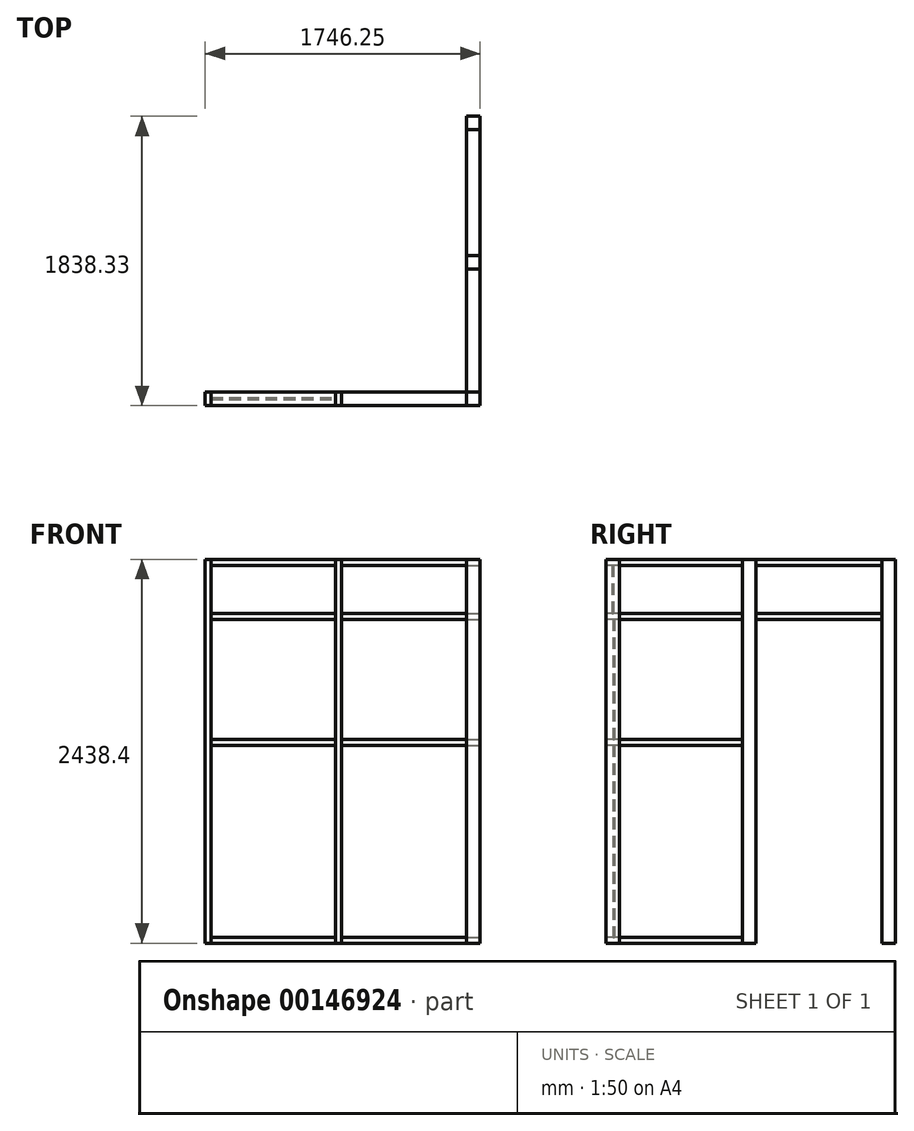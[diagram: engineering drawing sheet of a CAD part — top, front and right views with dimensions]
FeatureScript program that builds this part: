
annotation { "Feature Type Name" : "Feature", "Feature Type Description" : "" }
export const myFeature = defineFeature(function(context is Context, id is Id, definition is map)
    precondition{}
    {
        {
            var Q0;
            Q0=qCreatedBy(makeId("Top.planeOp"),FACE);
            var sketch = newSketch(context, id + "F0", { "sketchPlane" : qUnion([Q0])});
            skLineSegment(sketch, "E0.bottom", {"start": v(0, 0) * mm, "end": v(38.1, 0) * mm});
            skLineSegment(sketch, "E0.top", {"start": v(0, 85.73) * mm, "end": v(38.1, 85.73) * mm});
            skLineSegment(sketch, "E0.left", {"start": v(0, 0) * mm, "end": v(0, 85.73) * mm});
            skLineSegment(sketch, "E0.right", {"start": v(38.1, 0) * mm, "end": v(38.1, 85.73) * mm});
            skLineSegment(sketch, "E1", {"start": v(38.1, 0) * mm, "end": v(828.68, 0) * mm});
            skLineSegment(sketch, "E2.bottom", {"start": v(828.68, 0) * mm, "end": v(866.78, 0) * mm});
            skLineSegment(sketch, "E2.top", {"start": v(828.68, 85.73) * mm, "end": v(866.78, 85.73) * mm});
            skLineSegment(sketch, "E2.left", {"start": v(828.68, 0) * mm, "end": v(828.68, 85.73) * mm});
            skLineSegment(sketch, "E2.right", {"start": v(866.78, 0) * mm, "end": v(866.78, 85.73) * mm});
            skLineSegment(sketch, "E3", {"start": v(866.78, 0) * mm, "end": v(1660.53, 0) * mm});
            skLineSegment(sketch, "E4.bottom", {"start": v(1660.53, 0) * mm, "end": v(1746.25, 0) * mm});
            skLineSegment(sketch, "E4.top", {"start": v(1660.53, 85.73) * mm, "end": v(1746.25, 85.73) * mm});
            skLineSegment(sketch, "E4.left", {"start": v(1660.53, 0) * mm, "end": v(1660.53, 85.73) * mm});
            skLineSegment(sketch, "E4.right", {"start": v(1746.25, 0) * mm, "end": v(1746.25, 85.73) * mm});
            skLineSegment(sketch, "E5", {"start": v(1746.25, 85.72) * mm, "end": v(1746.25, 866.78) * mm});
            skLineSegment(sketch, "E6.bottom", {"start": v(1746.25, 866.78) * mm, "end": v(1660.53, 866.78) * mm});
            skLineSegment(sketch, "E6.top", {"start": v(1746.25, 952.5) * mm, "end": v(1660.53, 952.5) * mm});
            skLineSegment(sketch, "E6.left", {"start": v(1746.25, 866.78) * mm, "end": v(1746.25, 952.5) * mm});
            skLineSegment(sketch, "E6.right", {"start": v(1660.53, 866.78) * mm, "end": v(1660.53, 952.5) * mm});
            skLineSegment(sketch, "E7", {"start": v(1746.25, 952.5) * mm, "end": v(1746.25, 1752.6) * mm});
            skLineSegment(sketch, "E8.bottom", {"start": v(1746.25, 1752.6) * mm, "end": v(1660.52, 1752.6) * mm});
            skLineSegment(sketch, "E8.top", {"start": v(1746.25, 1838.33) * mm, "end": v(1660.53, 1838.33) * mm});
            skLineSegment(sketch, "E8.left", {"start": v(1746.25, 1752.6) * mm, "end": v(1746.25, 1838.33) * mm});
            skLineSegment(sketch, "E8.right", {"start": v(1660.52, 1752.6) * mm, "end": v(1660.52, 1838.33) * mm});
            skSolve(sketch);
        }
        {
            var Q0;
            Q0=makeQuery(id+"F0.imprint","IMPRINT",FACE,{"disambiguationData":[TD([[makeQuery(id+"F0.imprint","IMPRINT",EDGE,{"derivedFrom":sQuery(id+"F0.wireOp",EDGE,"E0.bottom")}),1.0]])]});
            var Q1;
            Q1=makeQuery(id+"F0.imprint","IMPRINT",FACE,{"disambiguationData":[TD([[makeQuery(id+"F0.imprint","IMPRINT",EDGE,{"derivedFrom":sQuery(id+"F0.wireOp",EDGE,"E2.bottom")}),1.0]])]});
            var Q2;
            Q2=makeQuery(id+"F0.imprint","IMPRINT",FACE,{"disambiguationData":[TD([[makeQuery(id+"F0.imprint","IMPRINT",EDGE,{"derivedFrom":sQuery(id+"F0.wireOp",EDGE,"E4.bottom")}),1.0]])]});
            var Q3;
            Q3=makeQuery(id+"F0.imprint","IMPRINT",FACE,{"disambiguationData":[TD([[makeQuery(id+"F0.imprint","IMPRINT",EDGE,{"derivedFrom":sQuery(id+"F0.wireOp",EDGE,"E6.bottom")}),-1.0]])]});
            var Q4;
            Q4=makeQuery(id+"F0.imprint","IMPRINT",FACE,{"disambiguationData":[TD([[makeQuery(id+"F0.imprint","IMPRINT",EDGE,{"derivedFrom":sQuery(id+"F0.wireOp",EDGE,"E8.bottom")}),-1.0]])]});
            extrude(context, id + "F1", {"entities" : qUnion([Q0, Q1, Q2, Q3, Q4]), "depth" : 2438.4 * mm});
        }
        {
            var Q0;
            Q0=makeQuery(id+"F1.opExtrude","SWEPT_FACE",FACE,{"disambiguationData":[OSD([sQuery(id+"F0.wireOp",EDGE,"E2.right")])]});
            var sketch = newSketch(context, id + "F2", { "sketchPlane" : qUnion([Q0])});
            skLineSegment(sketch, "E9", {"start": v(0, 0) * mm, "end": v(0, 38.1) * mm});
            skLineSegment(sketch, "E10", {"start": v(0, 38.1) * mm, "end": v(85.72, 38.1) * mm});
            skSolve(sketch);
        }
        {
            var Q0;
            Q0=makeQuery(id+"F1.opExtrude","SWEPT_FACE",FACE,{"disambiguationData":[OSD([sQuery(id+"F0.wireOp",EDGE,"E0.right")])]});
            var sketch = newSketch(context, id + "F3", { "sketchPlane" : qUnion([Q0])});
            skLineSegment(sketch, "E11", {"start": v(0, 0) * mm, "end": v(0, 38.1) * mm});
            skLineSegment(sketch, "E12", {"start": v(0, 38.1) * mm, "end": v(85.72, 38.1) * mm});
            skSolve(sketch);
        }
        {
            var Q0;
            Q0=makeQuery(id+"F3.imprint","IMPRINT",FACE,{"disambiguationData":[TD([[makeQuery(id+"F3.imprint","IMPRINT",EDGE,{"derivedFrom":sQuery(id+"F3.wireOp",EDGE,"E11")}),1.0]])]});
            extrude(context, id + "F4", {"entities" : qUnion([Q0]), "endBound" : BoundingType.UP_TO_NEXT, "depth" : 25.4 * mm});
        }
        {
            var Q0;
            Q0=makeQuery(id+"F2.imprint","IMPRINT",FACE,{"disambiguationData":[TD([[makeQuery(id+"F2.imprint","IMPRINT",EDGE,{"derivedFrom":sQuery(id+"F2.wireOp",EDGE,"E9")}),1.0]])]});
            extrude(context, id + "F5", {"entities" : qUnion([Q0]), "depth" : 793.75 * mm});
        }
        {
            var Q0;
            Q0=makeQuery(id+"F1.opExtrude","SWEPT_FACE",FACE,{"disambiguationData":[OSD([sQuery(id+"F0.wireOp",EDGE,"E4.top")])]});
            var sketch = newSketch(context, id + "F6", { "sketchPlane" : qUnion([Q0])});
            skLineSegment(sketch, "E13", {"start": v(-1746.25, 0) * mm, "end": v(-1746.25, 38.1) * mm});
            skLineSegment(sketch, "E14", {"start": v(-1746.25, 38.1) * mm, "end": v(-1660.53, 38.1) * mm});
            skSolve(sketch);
        }
        {
            var Q0;
            Q0=makeQuery(id+"F6.imprint","IMPRINT",FACE,{"disambiguationData":[TD([[makeQuery(id+"F6.imprint","IMPRINT",EDGE,{"derivedFrom":sQuery(id+"F6.wireOp",EDGE,"E13")}),1.0]])]});
            extrude(context, id + "F7", {"entities" : qUnion([Q0]), "endBound" : BoundingType.UP_TO_NEXT, "depth" : 25.4 * mm});
        }
        {
            var Q0;
            Q0=makeQuery(id+"F1.opExtrude","SWEPT_FACE",FACE,{"disambiguationData":[OSD([sQuery(id+"F0.wireOp",EDGE,"E4.top")])]});
            var sketch = newSketch(context, id + "F8", { "sketchPlane" : qUnion([Q0])});
            skLineSegment(sketch, "E15", {"start": v(-1746.25, 2438.4) * mm, "end": v(-1746.25, 2400.3) * mm});
            skLineSegment(sketch, "E16", {"start": v(-1746.25, 2400.3) * mm, "end": v(-1660.53, 2400.3) * mm});
            skSolve(sketch);
        }
        {
            var Q0;
            Q0=makeQuery(id+"F8.imprint","IMPRINT",FACE,{"disambiguationData":[TD([[makeQuery(id+"F8.imprint","IMPRINT",EDGE,{"derivedFrom":sQuery(id+"F8.wireOp",EDGE,"E15")}),1.0]])]});
            extrude(context, id + "F9", {"entities" : qUnion([Q0]), "endBound" : BoundingType.UP_TO_NEXT, "depth" : 25.4 * mm});
        }
        {
            var Q0;
            Q0=makeQuery(id+"F1.opExtrude","SWEPT_FACE",FACE,{"disambiguationData":[OSD([sQuery(id+"F0.wireOp",EDGE,"E2.right")])]});
            var sketch = newSketch(context, id + "F10", { "sketchPlane" : qUnion([Q0])});
            skLineSegment(sketch, "E17", {"start": v(0, 2438.4) * mm, "end": v(0, 2400.3) * mm});
            skLineSegment(sketch, "E18", {"start": v(0, 2400.3) * mm, "end": v(85.72, 2400.3) * mm});
            skSolve(sketch);
        }
        {
            var Q0;
            Q0=makeQuery(id+"F10.imprint","IMPRINT",FACE,{"disambiguationData":[TD([[makeQuery(id+"F10.imprint","IMPRINT",EDGE,{"derivedFrom":sQuery(id+"F10.wireOp",EDGE,"E17")}),1.0]])]});
            extrude(context, id + "F11", {"entities" : qUnion([Q0]), "endBound" : BoundingType.UP_TO_NEXT, "depth" : 25.4 * mm});
        }
        {
            var Q0;
            Q0=makeQuery(id+"F1.opExtrude","SWEPT_FACE",FACE,{"disambiguationData":[OSD([sQuery(id+"F0.wireOp",EDGE,"E0.right")])]});
            var sketch = newSketch(context, id + "F12", { "sketchPlane" : qUnion([Q0])});
            skLineSegment(sketch, "E19", {"start": v(0, 2438.4) * mm, "end": v(0, 2400.3) * mm});
            skLineSegment(sketch, "E20", {"start": v(0, 2400.3) * mm, "end": v(85.72, 2400.3) * mm});
            skSolve(sketch);
        }
        {
            var Q0;
            Q0=makeQuery(id+"F12.imprint","IMPRINT",FACE,{"disambiguationData":[TD([[makeQuery(id+"F12.imprint","IMPRINT",EDGE,{"derivedFrom":sQuery(id+"F12.wireOp",EDGE,"E19")}),1.0]])]});
            extrude(context, id + "F13", {"entities" : qUnion([Q0]), "endBound" : BoundingType.UP_TO_NEXT, "depth" : 25.4 * mm});
        }
        {
            var Q0;
            Q0=makeQuery(id+"F1.opExtrude","SWEPT_FACE",FACE,{"disambiguationData":[OSD([sQuery(id+"F0.wireOp",EDGE,"E6.top")])]});
            var sketch = newSketch(context, id + "F14", { "sketchPlane" : qUnion([Q0])});
            skLineSegment(sketch, "E21", {"start": v(-1746.25, 2438.4) * mm, "end": v(-1746.25, 2400.3) * mm});
            skLineSegment(sketch, "E22", {"start": v(-1746.25, 2400.3) * mm, "end": v(-1660.53, 2400.3) * mm});
            skSolve(sketch);
        }
        {
            var Q0;
            Q0=makeQuery(id+"F14.imprint","IMPRINT",FACE,{"disambiguationData":[TD([[makeQuery(id+"F14.imprint","IMPRINT",EDGE,{"derivedFrom":sQuery(id+"F14.wireOp",EDGE,"E21")}),1.0]])]});
            extrude(context, id + "F15", {"entities" : qUnion([Q0]), "endBound" : BoundingType.UP_TO_NEXT, "depth" : 25.4 * mm});
        }
        {
            var Q0;
            Q0=makeQuery(id+"F1.opExtrude","SWEPT_FACE",FACE,{"disambiguationData":[OSD([sQuery(id+"F0.wireOp",EDGE,"E0.right")])]});
            var sketch = newSketch(context, id + "F16", { "sketchPlane" : qUnion([Q0])});
            skLineSegment(sketch, "E23", {"start": v(0, 2438.4) * mm, "end": v(0, 2095.5) * mm});
            skLineSegment(sketch, "E24.bottom", {"start": v(0, 2095.5) * mm, "end": v(85.72, 2095.5) * mm});
            skLineSegment(sketch, "E24.top", {"start": v(0, 2057.4) * mm, "end": v(85.72, 2057.4) * mm});
            skLineSegment(sketch, "E24.left", {"start": v(0, 2095.5) * mm, "end": v(0, 2057.4) * mm});
            skLineSegment(sketch, "E24.right", {"start": v(85.72, 2095.5) * mm, "end": v(85.72, 2057.4) * mm});
            skSolve(sketch);
        }
        {
            var Q0;
            Q0=makeQuery(id+"F16.imprint","IMPRINT",FACE,{"disambiguationData":[TD([[makeQuery(id+"F16.imprint","IMPRINT",EDGE,{"derivedFrom":sQuery(id+"F16.wireOp",EDGE,"E24.bottom")}),-1.0]])]});
            extrude(context, id + "F17", {"entities" : qUnion([Q0]), "endBound" : BoundingType.UP_TO_NEXT, "depth" : 25.4 * mm});
        }
        {
            var Q0;
            Q0=makeQuery(id+"F1.opExtrude","SWEPT_FACE",FACE,{"disambiguationData":[OSD([sQuery(id+"F0.wireOp",EDGE,"E2.right")])]});
            var sketch = newSketch(context, id + "F18", { "sketchPlane" : qUnion([Q0])});
            skLineSegment(sketch, "E25", {"start": v(0, 2438.4) * mm, "end": v(0, 2095.5) * mm});
            skLineSegment(sketch, "E26.bottom", {"start": v(0, 2095.5) * mm, "end": v(85.72, 2095.5) * mm});
            skLineSegment(sketch, "E26.top", {"start": v(0, 2057.4) * mm, "end": v(85.72, 2057.4) * mm});
            skLineSegment(sketch, "E26.left", {"start": v(0, 2095.5) * mm, "end": v(0, 2057.4) * mm});
            skLineSegment(sketch, "E26.right", {"start": v(85.72, 2095.5) * mm, "end": v(85.72, 2057.4) * mm});
            skSolve(sketch);
        }
        {
            var Q0;
            Q0=makeQuery(id+"F18.imprint","IMPRINT",FACE,{"disambiguationData":[TD([[makeQuery(id+"F18.imprint","IMPRINT",EDGE,{"derivedFrom":sQuery(id+"F18.wireOp",EDGE,"E26.bottom")}),-1.0]])]});
            extrude(context, id + "F19", {"entities" : qUnion([Q0]), "endBound" : BoundingType.UP_TO_NEXT, "depth" : 25.4 * mm});
        }
        {
            var Q0;
            Q0=makeQuery(id+"F1.opExtrude","SWEPT_FACE",FACE,{"disambiguationData":[OSD([sQuery(id+"F0.wireOp",EDGE,"E4.top")])]});
            var sketch = newSketch(context, id + "F20", { "sketchPlane" : qUnion([Q0])});
            skLineSegment(sketch, "E27", {"start": v(-1746.25, 2438.4) * mm, "end": v(-1746.25, 2095.5) * mm});
            skLineSegment(sketch, "E28.bottom", {"start": v(-1746.25, 2095.5) * mm, "end": v(-1660.53, 2095.5) * mm});
            skLineSegment(sketch, "E28.top", {"start": v(-1746.25, 2057.4) * mm, "end": v(-1660.53, 2057.4) * mm});
            skLineSegment(sketch, "E28.left", {"start": v(-1746.25, 2095.5) * mm, "end": v(-1746.25, 2057.4) * mm});
            skLineSegment(sketch, "E28.right", {"start": v(-1660.53, 2095.5) * mm, "end": v(-1660.53, 2057.4) * mm});
            skSolve(sketch);
        }
        {
            var Q0;
            Q0 = qSketchRegion(id + "F20", true);
            extrude(context, id + "F21", {"entities" : qUnion([Q0]), "endBound" : BoundingType.UP_TO_NEXT, "depth" : 25.4 * mm});
        }
        {
            var Q0;
            Q0=makeQuery(id+"F1.opExtrude","SWEPT_FACE",FACE,{"disambiguationData":[OSD([sQuery(id+"F0.wireOp",EDGE,"E6.top")])]});
            var sketch = newSketch(context, id + "F22", { "sketchPlane" : qUnion([Q0])});
            skLineSegment(sketch, "E29", {"start": v(-1746.25, 2438.4) * mm, "end": v(-1746.25, 2095.5) * mm});
            skLineSegment(sketch, "E30.bottom", {"start": v(-1746.25, 2095.5) * mm, "end": v(-1660.53, 2095.5) * mm});
            skLineSegment(sketch, "E30.top", {"start": v(-1746.25, 2057.4) * mm, "end": v(-1660.53, 2057.4) * mm});
            skLineSegment(sketch, "E30.left", {"start": v(-1746.25, 2095.5) * mm, "end": v(-1746.25, 2057.4) * mm});
            skLineSegment(sketch, "E30.right", {"start": v(-1660.53, 2095.5) * mm, "end": v(-1660.53, 2057.4) * mm});
            skSolve(sketch);
        }
        {
            var Q0;
            Q0 = qSketchRegion(id + "F22", true);
            extrude(context, id + "F23", {"entities" : qUnion([Q0]), "endBound" : BoundingType.UP_TO_NEXT, "depth" : 25.4 * mm});
        }
        {
            var Q0;
            Q0=makeQuery(id+"F1.opExtrude","SWEPT_FACE",FACE,{"disambiguationData":[OSD([sQuery(id+"F0.wireOp",EDGE,"E4.top")])]});
            var sketch = newSketch(context, id + "F24", { "sketchPlane" : qUnion([Q0])});
            skLineSegment(sketch, "E31", {"start": v(-1746.25, 0) * mm, "end": v(-1746.25, 1257.3) * mm});
            skLineSegment(sketch, "E32.bottom", {"start": v(-1746.25, 1257.3) * mm, "end": v(-1660.53, 1257.3) * mm});
            skLineSegment(sketch, "E32.top", {"start": v(-1746.25, 1295.4) * mm, "end": v(-1660.53, 1295.4) * mm});
            skLineSegment(sketch, "E32.left", {"start": v(-1746.25, 1257.3) * mm, "end": v(-1746.25, 1295.4) * mm});
            skLineSegment(sketch, "E32.right", {"start": v(-1660.53, 1257.3) * mm, "end": v(-1660.53, 1295.4) * mm});
            skSolve(sketch);
        }
        {
            var Q0;
            Q0 = qSketchRegion(id + "F24", true);
            extrude(context, id + "F25", {"entities" : qUnion([Q0]), "endBound" : BoundingType.UP_TO_NEXT, "depth" : 25.4 * mm});
        }
        {
            var Q0;
            Q0=makeQuery(id+"F1.opExtrude","SWEPT_FACE",FACE,{"disambiguationData":[OSD([sQuery(id+"F0.wireOp",EDGE,"E2.right")])]});
            var sketch = newSketch(context, id + "F26", { "sketchPlane" : qUnion([Q0])});
            skLineSegment(sketch, "E33", {"start": v(0, 0) * mm, "end": v(0, 1257.3) * mm});
            skLineSegment(sketch, "E34.bottom", {"start": v(0, 1257.3) * mm, "end": v(85.72, 1257.3) * mm});
            skLineSegment(sketch, "E34.top", {"start": v(0, 1295.4) * mm, "end": v(85.72, 1295.4) * mm});
            skLineSegment(sketch, "E34.left", {"start": v(0, 1257.3) * mm, "end": v(0, 1295.4) * mm});
            skLineSegment(sketch, "E34.right", {"start": v(85.72, 1257.3) * mm, "end": v(85.72, 1295.4) * mm});
            skSolve(sketch);
        }
        {
            var Q0;
            Q0 = qSketchRegion(id + "F26", true);
            extrude(context, id + "F27", {"entities" : qUnion([Q0]), "endBound" : BoundingType.UP_TO_NEXT, "depth" : 25.4 * mm});
        }
        {
            var Q0;
            Q0=makeQuery(id+"F1.opExtrude","SWEPT_FACE",FACE,{"disambiguationData":[OSD([sQuery(id+"F0.wireOp",EDGE,"E0.right")])]});
            var sketch = newSketch(context, id + "F28", { "sketchPlane" : qUnion([Q0])});
            skLineSegment(sketch, "E35", {"start": v(0, 0) * mm, "end": v(0, 1257.3) * mm});
            skLineSegment(sketch, "E36.bottom", {"start": v(0, 1257.3) * mm, "end": v(85.72, 1257.3) * mm});
            skLineSegment(sketch, "E36.top", {"start": v(0, 1295.4) * mm, "end": v(85.72, 1295.4) * mm});
            skLineSegment(sketch, "E36.left", {"start": v(0, 1257.3) * mm, "end": v(0, 1295.4) * mm});
            skLineSegment(sketch, "E36.right", {"start": v(85.72, 1257.3) * mm, "end": v(85.72, 1295.4) * mm});
            skSolve(sketch);
        }
        {
            var Q0;
            Q0 = qSketchRegion(id + "F28", true);
            extrude(context, id + "F29", {"entities" : qUnion([Q0]), "endBound" : BoundingType.UP_TO_NEXT, "depth" : 25.4 * mm});
        }
        {
            var Q0;
            Q0=makeQuery(id+"F4.opExtrude","SWEPT_FACE",FACE,{"disambiguationData":[OSD([sQuery(id+"F3.wireOp",EDGE,"E12")])]});
            var sketch = newSketch(context, id + "F30", { "sketchPlane" : qUnion([Q0])});
            skLineSegment(sketch, "E37", {"start": v(38.1, 0) * mm, "end": v(38.1, 42.86) * mm});
            skLineSegment(sketch, "E38.bottom", {"start": v(38.1, 42.86) * mm, "end": v(828.68, 42.86) * mm});
            skLineSegment(sketch, "E38.top", {"start": v(38.1, 52.39) * mm, "end": v(828.68, 52.39) * mm});
            skLineSegment(sketch, "E38.left", {"start": v(38.1, 42.86) * mm, "end": v(38.1, 52.39) * mm});
            skLineSegment(sketch, "E38.right", {"start": v(828.68, 42.86) * mm, "end": v(828.68, 52.39) * mm});
            skSolve(sketch);
        }
        {
            var Q0;
            Q0=makeQuery(id+"F30.imprint","IMPRINT",FACE,{"disambiguationData":[TD([[makeQuery(id+"F30.imprint","IMPRINT",EDGE,{"derivedFrom":sQuery(id+"F30.wireOp",EDGE,"E38.bottom")}),1.0]])]});
            extrude(context, id + "F31", {"entities" : qUnion([Q0]), "endBound" : BoundingType.UP_TO_NEXT, "depth" : 25.4 * mm});
        }
        {
            var Q0;
            Q0=makeQuery(id+"F29.opExtrude","SWEPT_FACE",FACE,{"disambiguationData":[OSD([sQuery(id+"F28.wireOp",EDGE,"E36.top")])]});
            var sketch = newSketch(context, id + "F32", { "sketchPlane" : qUnion([Q0])});
            skLineSegment(sketch, "E39", {"start": v(38.1, 0) * mm, "end": v(38.1, 42.86) * mm});
            skLineSegment(sketch, "E40.bottom", {"start": v(38.1, 42.86) * mm, "end": v(828.68, 42.86) * mm});
            skLineSegment(sketch, "E40.top", {"start": v(38.1, 52.39) * mm, "end": v(828.68, 52.39) * mm});
            skLineSegment(sketch, "E40.left", {"start": v(38.1, 42.86) * mm, "end": v(38.1, 52.39) * mm});
            skLineSegment(sketch, "E40.right", {"start": v(828.68, 42.86) * mm, "end": v(828.68, 52.39) * mm});
            skSolve(sketch);
        }
        {
            var Q0;
            Q0 = qSketchRegion(id + "F32", true);
            extrude(context, id + "F33", {"entities" : qUnion([Q0]), "endBound" : BoundingType.UP_TO_NEXT, "depth" : 25.4 * mm});
        }
        {
            var Q0;
            Q0=makeQuery(id+"F17.opExtrude","SWEPT_FACE",FACE,{"disambiguationData":[OSD([sQuery(id+"F16.wireOp",EDGE,"E24.bottom")])]});
            var sketch = newSketch(context, id + "F34", { "sketchPlane" : qUnion([Q0])});
            skLineSegment(sketch, "E41", {"start": v(38.1, 0) * mm, "end": v(38.1, 38.1) * mm});
            skLineSegment(sketch, "E42.bottom", {"start": v(38.1, 38.1) * mm, "end": v(828.68, 38.1) * mm});
            skLineSegment(sketch, "E42.top", {"start": v(38.1, 47.63) * mm, "end": v(828.68, 47.63) * mm});
            skLineSegment(sketch, "E42.left", {"start": v(38.1, 38.1) * mm, "end": v(38.1, 47.63) * mm});
            skLineSegment(sketch, "E42.right", {"start": v(828.68, 38.1) * mm, "end": v(828.68, 47.63) * mm});
            skSolve(sketch);
        }
        {
            var Q0;
            Q0=makeQuery(id+"F34.imprint","IMPRINT",FACE,{"disambiguationData":[TD([[makeQuery(id+"F34.imprint","IMPRINT",EDGE,{"derivedFrom":sQuery(id+"F34.wireOp",EDGE,"E42.bottom")}),1.0]])]});
            extrude(context, id + "F35", {"entities" : qUnion([Q0]), "endBound" : BoundingType.UP_TO_NEXT, "depth" : 25.4 * mm});
        }
    });
